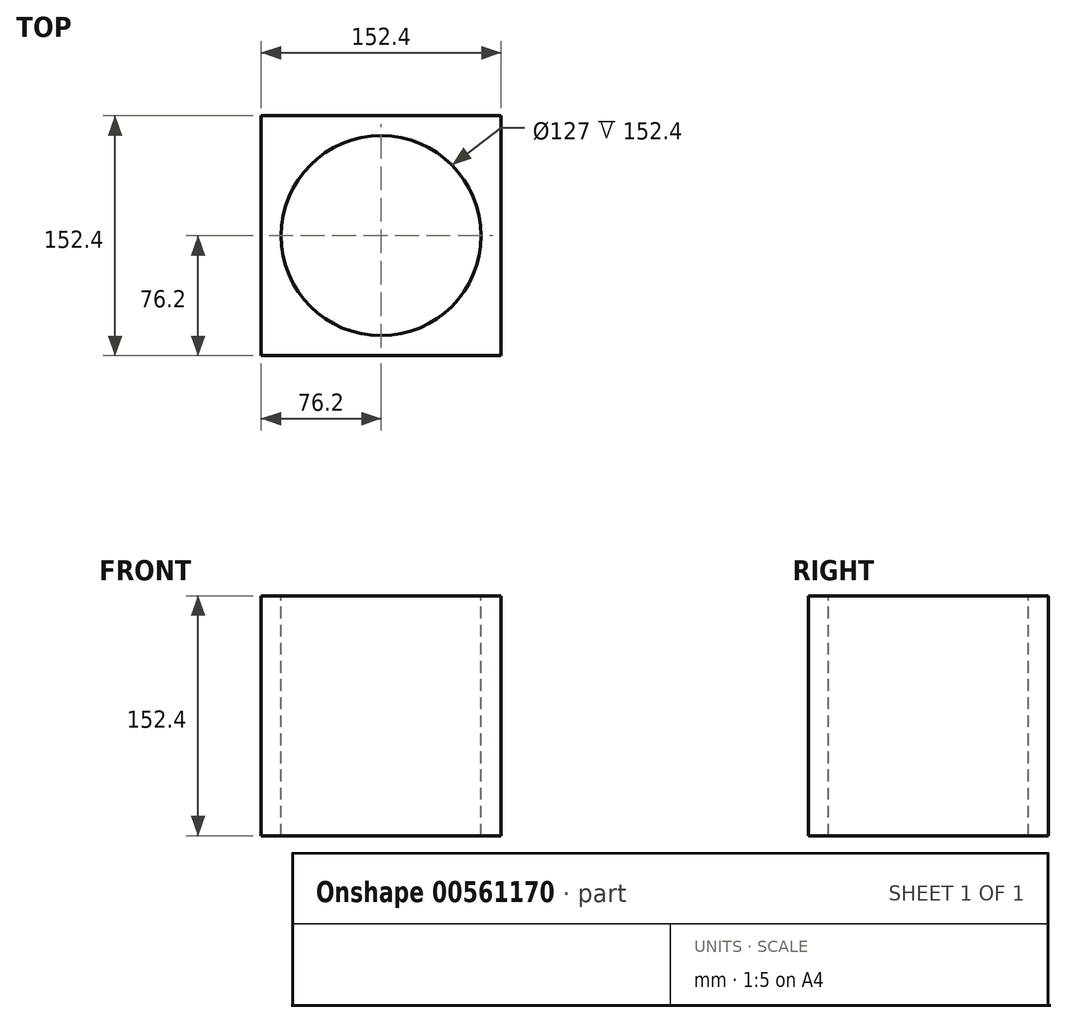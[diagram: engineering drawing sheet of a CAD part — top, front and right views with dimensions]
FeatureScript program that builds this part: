
annotation { "Feature Type Name" : "Feature", "Feature Type Description" : "" }
export const myFeature = defineFeature(function(context is Context, id is Id, definition is map)
    precondition{}
    {
        {
            var Q0;
            Q0=qCreatedBy(makeId("Front.planeOp"),FACE);
            var sketch = newSketch(context, id + "F0", { "sketchPlane" : qUnion([Q0])});
            skLineSegment(sketch, "E0.bottom", {"start": v(-76.2, 76.2) * mm, "end": v(76.2, 76.2) * mm});
            skLineSegment(sketch, "E0.top", {"start": v(-76.2, -76.2) * mm, "end": v(76.2, -76.2) * mm});
            skLineSegment(sketch, "E0.left", {"start": v(-76.2, 76.2) * mm, "end": v(-76.2, -76.2) * mm});
            skLineSegment(sketch, "E0.right", {"start": v(76.2, 76.2) * mm, "end": v(76.2, -76.2) * mm});
            skPoint(sketch, "E0.middle", {"position": v(0, 0) * mm});
            skSolve(sketch);
        }
        {
            var Q0;
            Q0 = qSketchRegion(id + "F0", true);
            extrude(context, id + "F1", {"entities" : qUnion([Q0]), "oppositeDirection" : true, "depth" : 152.4 * mm, "offsetDistance" : 25.4 * mm});
        }
        {
            var Q0;
            Q0=makeQuery(id+"F1.opExtrude","SWEPT_FACE",FACE,{"disambiguationData":[OSD([sQuery(id+"F0.wireOp",EDGE,"E0.bottom")])]});
            var sketch = newSketch(context, id + "F2", { "sketchPlane" : qUnion([Q0])});
            skPoint(sketch, "E1.centerSnap0", {"position": v(-76.2, 76.2) * mm});
            skPoint(sketch, "E1.centerSnap1", {"position": v(0, 0) * mm});
            skCircle(sketch, "E2", {"center": v(0, 76.2) * mm, "radius": 63.5 * mm});
            skSolve(sketch);
        }
        {
            var Q0;
            Q0 = qSketchRegion(id + "F2", true);
            extrude(context, id + "F3", {"entities" : qUnion([Q0]), "operationType" : NewBodyOperationType.REMOVE, "endBound" : BoundingType.THROUGH_ALL, "oppositeDirection" : true, "depth" : 152.4 * mm, "offsetDistance" : 25.4 * mm});
        }
    });
